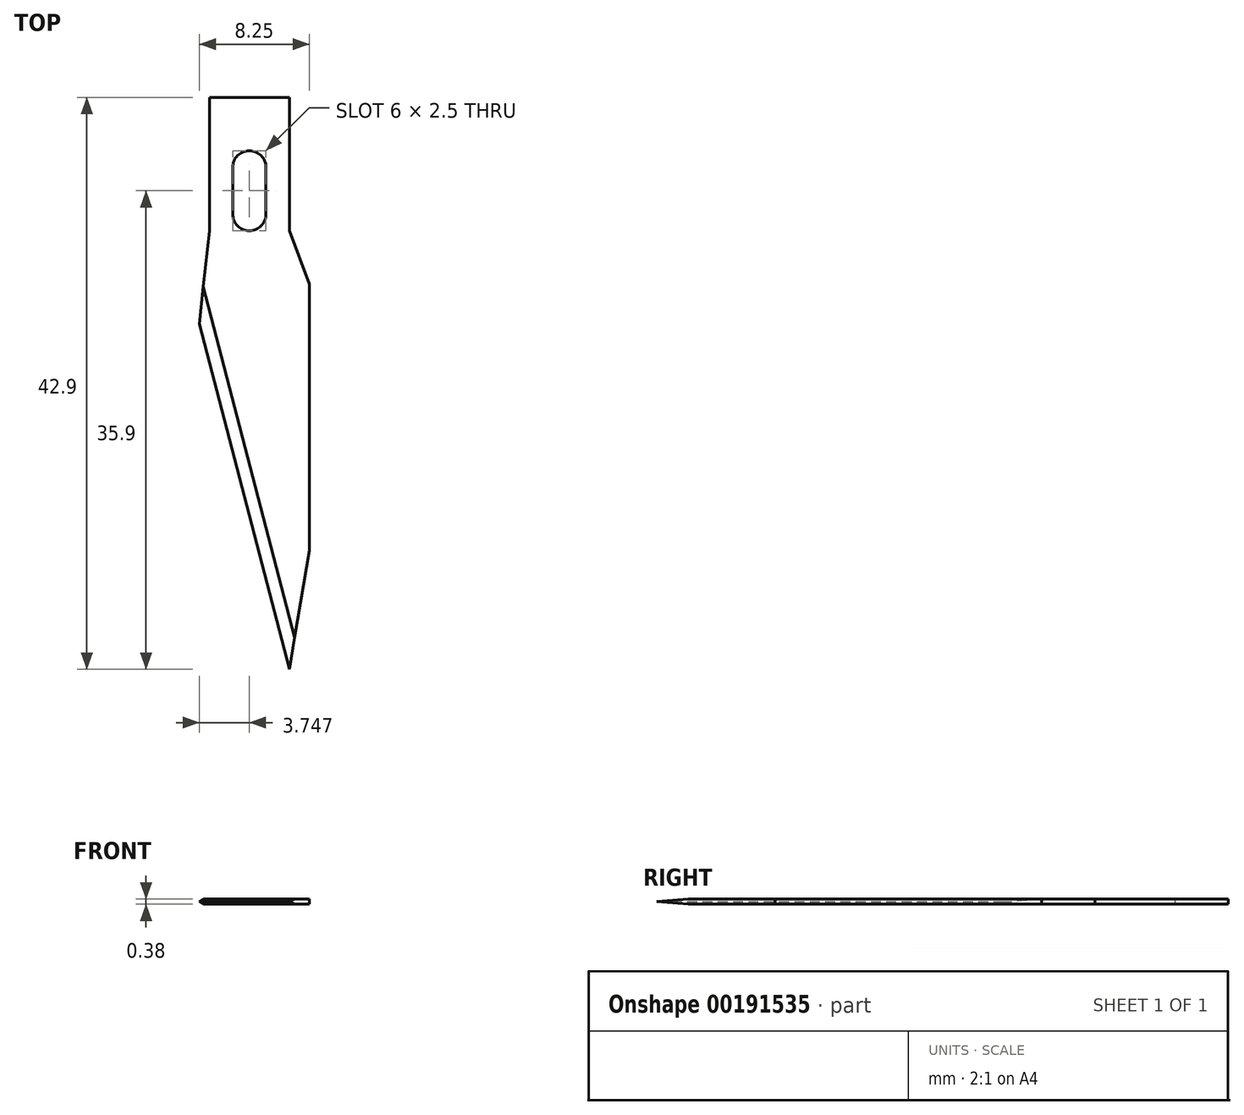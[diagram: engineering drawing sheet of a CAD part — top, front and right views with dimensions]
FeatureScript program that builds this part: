
annotation { "Feature Type Name" : "Feature", "Feature Type Description" : "" }
export const myFeature = defineFeature(function(context is Context, id is Id, definition is map)
    precondition{}
    {
        {
            var Q0;
            Q0=qCreatedBy(makeId("Top.planeOp"),FACE);
            var sketch = newSketch(context, id + "F0", { "sketchPlane" : qUnion([Q0])});
            skLineSegment(sketch, "E0", {"start": v(0, 0) * mm, "end": v(0, 20) * mm});
            skLineSegment(sketch, "E1", {"start": v(0, 20) * mm, "end": v(-1.5, 24) * mm});
            skLineSegment(sketch, "E2", {"start": v(-1.5, 24) * mm, "end": v(-1.5, 34) * mm});
            skLineSegment(sketch, "E3", {"start": v(-1.5, 34) * mm, "end": v(-7.5, 34) * mm});
            skLineSegment(sketch, "E4", {"start": v(-7.5, 34) * mm, "end": v(-7.5, 24) * mm});
            skLineSegment(sketch, "E5", {"start": v(-7.5, 24) * mm, "end": v(-8.26, 17) * mm});
            skLineSegment(sketch, "E6", {"start": v(-8.26, 17) * mm, "end": v(-1.5, -8.9) * mm});
            skLineSegment(sketch, "E7", {"start": v(-1.5, -8.9) * mm, "end": v(0, 0) * mm});
            skCircle(sketch, "E8", {"center": v(-4.5, 28.75) * mm, "radius": 1.25 * mm});
            skLineSegment(sketch, "E9.bottom", {"start": v(-3.25, 28.75) * mm, "end": v(-5.75, 28.75) * mm});
            skLineSegment(sketch, "E9.top", {"start": v(-3.25, 25.25) * mm, "end": v(-5.75, 25.25) * mm});
            skLineSegment(sketch, "E9.left", {"start": v(-3.25, 28.75) * mm, "end": v(-3.25, 25.25) * mm});
            skLineSegment(sketch, "E9.right", {"start": v(-5.75, 28.75) * mm, "end": v(-5.75, 25.25) * mm});
            skCircle(sketch, "E10", {"center": v(-4.5, 25.25) * mm, "radius": 1.25 * mm});
            skSolve(sketch);
        }
        {
            var Q0;
            Q0 = qSketchRegion(id + "F0", true);
            extrude(context, id + "F1", {"entities" : qUnion([Q0]), "depth" : .38 * mm});
        }
        {
            var Q0;
            Q0=makeQuery(id+"F1.opExtrude","CAP_EDGE",EDGE,{"disambiguationData":[OSD([sQuery(id+"F0.wireOp",EDGE,"E6")])],"isStart":true});
            var Q1;
            Q1=makeQuery(id+"F1.opExtrude","CAP_EDGE",EDGE,{"disambiguationData":[OSD([sQuery(id+"F0.wireOp",EDGE,"E6")])],"isStart":false});
            chamfer(context, id + "F2", {"entities" : qUnion([Q0, Q1]), "chamferType" : ChamferType.TWO_OFFSETS, "width1" : 0.2 * mm, "oppositeDirection" : false, "width2" : 1 * mm, "tangentPropagation" : true});
        }
    });
